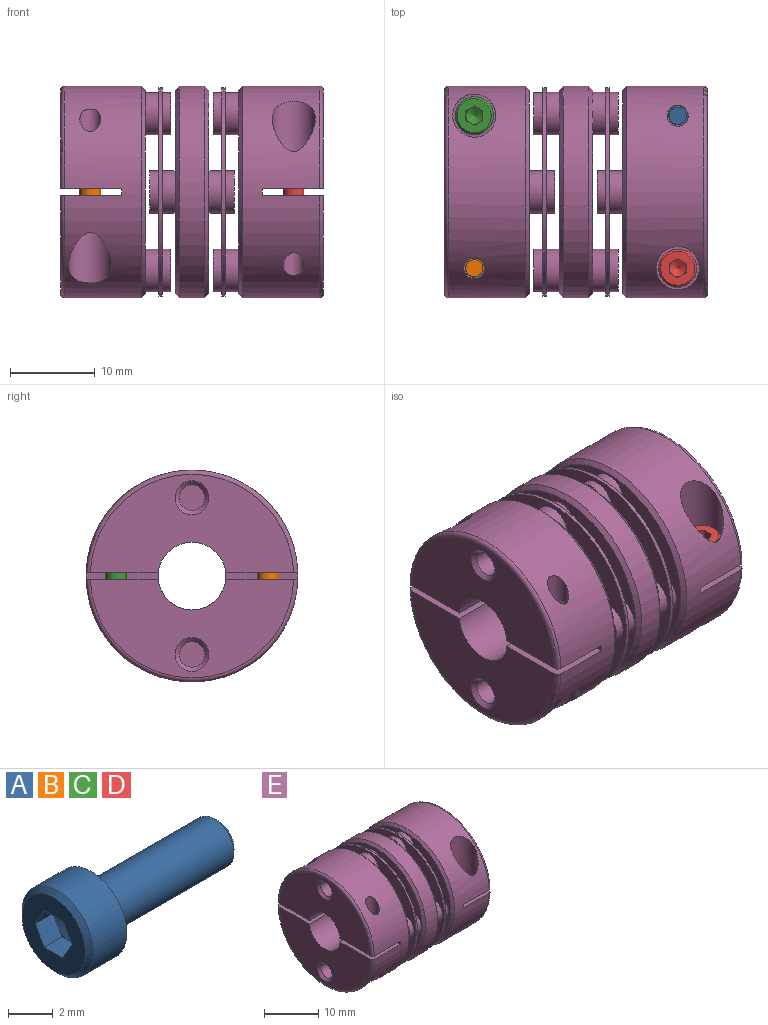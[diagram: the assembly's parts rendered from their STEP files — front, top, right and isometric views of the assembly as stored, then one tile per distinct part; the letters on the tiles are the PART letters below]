
ASSEMBLY  parts=5 mates=4
PART A: 20 faces, bbox 10.4x4.5x4.5 mm
  f0: plane 0.87x0.5mm, normal (-1,0,0), area 0.1mm2, adj f13,f14,f19
  f1: plane 1x0.29mm, normal (-1,0,0), area 0.1mm2, adj f13,f18,f19
  f2: plane 0.87x0.5mm, normal (-1,0,0), area 0.1mm2, adj f17,f18,f19
  f3: plane 0.87x0.5mm, normal (-1,0,0), area 0.1mm2, adj f16,f17,f19
  f4: plane 1x0.29mm, normal (-1,0,0), area 0.1mm2, adj f15,f16,f19
  f5: plane 0.87x0.5mm, normal (-1,0,0), area 0.1mm2, adj f14,f15,f19
  f6: plane 4x4mm, normal (-1,0,0), area 9.1mm2, adj f7,f13,f14,f15,f16,f17,f18
  f7: cone r=2.25mm half-angle=45deg, axis (1,0,0), area 4.7mm2, adj f6,f8
  f8: cylinder r=2.25mm len=4.5mm, axis (-1,0,0), area 29.8mm2, adj f7,f9
  f9: plane 4.5x4.5mm, normal (1,0,0), area 11mm2, adj f8,f10
  f10: cylinder r=1.25mm len=7.76mm, axis (-1,0,0), area 60.9mm2, adj f9,f11
  f11: cone r=1.01mm half-angle=45deg, axis (-1,0,0), area 2.4mm2, adj f10,f12
  f12: plane 2.01x2.01mm, normal (1,0,0), area 3.2mm2, adj f11
  f13: plane 1.1x1mm, normal (0,-0.87,-0.5), area 1.3mm2, adj f0,f1,f6,f14,f18
  f14: plane 1.15x1.1mm, normal (0,0,-1), area 1.3mm2, adj f0,f5,f6,f13,f15
  f15: plane 1.1x1mm, normal (0,0.87,-0.5), area 1.3mm2, adj f4,f5,f6,f14,f16
  f16: plane 1.1x1mm, normal (0,0.87,0.5), area 1.3mm2, adj f3,f4,f6,f15,f17
  f17: plane 1.15x1.1mm, normal (0,0,1), area 1.3mm2, adj f2,f3,f6,f16,f18
  f18: plane 1.1x1mm, normal (0,-0.87,0.5), area 1.3mm2, adj f1,f2,f6,f13,f17
  f19: cone r=0mm half-angle=60deg, axis (-1,0,0), area 3.6mm2, adj f0,f1,f2,f3,f4,f5
PART B: same geometry as A
PART C: same geometry as A
PART D: same geometry as A
PART E: 106 faces, bbox 31x27.1x27.1 mm
  f0: cylinder r=12.5mm len=25mm, axis (-1,0,0), area 619.5mm2, adj f1,f2,f3,f4,f14,f58,f61,f64
  f1: plane 8.52x7.21mm, normal (0,0,-1), area 56.3mm2, adj f0,f13,f60,f61,f64,f104
  f2: plane 8.52x7.21mm, normal (0,0,1), area 56.3mm2, adj f0,f12,f14,f60,f64,f99
  f3: plane 8.52x7.21mm, normal (0,0,1), area 56.3mm2, adj f0,f12,f14,f60,f65,f97
  f4: plane 8.52x7.21mm, normal (0,0,-1), area 56.3mm2, adj f0,f13,f60,f61,f65,f92
  f5: cylinder r=12.5mm len=25mm, axis (-1,0,0), area 619.5mm2, adj f6,f7,f8,f9,f16,f17,f24,f62
  f6: plane 8.52x7.21mm, normal (0,0,1), area 56.3mm2, adj f5,f10,f15,f17,f62,f91
  f7: plane 8.52x7.21mm, normal (0,0,-1), area 56.3mm2, adj f5,f11,f15,f16,f62,f87
  f8: plane 8.52x7.21mm, normal (0,0,-1), area 56.3mm2, adj f5,f11,f15,f16,f63,f84
  f9: plane 8.52x7.21mm, normal (0,0,1), area 56.3mm2, adj f5,f10,f15,f17,f63,f80
  f10: plane 23.99x11.6mm, normal (-1,0,0), area 182.1mm2, adj f6,f9,f15,f17,f75
  f11: plane 23.99x11.6mm, normal (-1,0,0), area 182.1mm2, adj f7,f8,f15,f16,f72
  f12: plane 23.99x11.6mm, normal (1,0,0), area 182.1mm2, adj f2,f3,f14,f60,f71
  f13: plane 23.99x11.6mm, normal (1,0,0), area 182.1mm2, adj f1,f4,f60,f61,f68
  f14: torus R=12mm, axis (-1,0,0), area 29.8mm2, adj f0,f2,f3,f12
  f15: cylinder r=4mm len=10mm, axis (-1,0,0), area 239.8mm2, adj f6,f7,f8,f9,f10,f11,f23,f62
  f16: torus R=12mm, axis (-1,0,0), area 29.8mm2, adj f5,f7,f8,f11
  f17: torus R=12mm, axis (-1,0,0), area 29.8mm2, adj f5,f6,f9,f10
  f18: cylinder r=2.5mm len=5mm, axis (-1,0,0), area 23.6mm2, adj f20,f44
  f19: cylinder r=2.5mm len=5mm, axis (-1,0,0), area 23.6mm2, adj f20,f44
  f20: plane 24x24mm, normal (1,0,0), area 290.4mm2, adj f18,f19,f40,f41
  f21: cylinder r=2.5mm len=5mm, axis (-1,0,0), area 25.1mm2, adj f23,f25
  f22: cylinder r=2.5mm len=5mm, axis (-1,0,0), area 25.1mm2, adj f23,f25
  f23: plane 24x24mm, normal (1,0,0), area 362.9mm2, adj f15,f21,f22,f24
  f24: cone r=12mm half-angle=45deg, axis (-1,0,0), area 54.4mm2, adj f5,f23
  f25: plane 24.6x24.6mm, normal (-1,0,0), area 274mm2, adj f21,f22,f27,f28,f34,f37
  f26: plane 24.6x24.6mm, normal (1,0,0), area 274mm2, adj f27,f28,f30,f32,f33,f36
  f27: cylinder r=12.3mm len=24.6mm, axis (-1,0,0), area 30.9mm2, adj f25,f26
  f28: cylinder r=6.25mm len=12.5mm, axis (-1,0,0), area 15.7mm2, adj f25,f26
  f29: plane 5x5mm, normal (1,0,0), area 19.6mm2, adj f30
  f30: cylinder r=2.5mm len=5mm, axis (-1,0,0), area 15.7mm2, adj f26,f29
  f31: plane 5x5mm, normal (1,0,0), area 19.6mm2, adj f32
  f32: cylinder r=2.5mm len=5mm, axis (-1,0,0), area 15.7mm2, adj f26,f31
  f33: cylinder r=2.5mm len=5mm, axis (1,0,0), area 23.6mm2, adj f26,f39
  f34: cylinder r=2.5mm len=5mm, axis (1,0,0), area 17.3mm2, adj f25,f35
  f35: plane 5x5mm, normal (-1,0,0), area 19.6mm2, adj f34
  f36: cylinder r=2.5mm len=5mm, axis (1,0,0), area 23.6mm2, adj f26,f39
  f37: cylinder r=2.5mm len=5mm, axis (1,0,0), area 17.3mm2, adj f25,f38
  f38: plane 5x5mm, normal (-1,0,0), area 19.6mm2, adj f37
  f39: plane 24x24mm, normal (-1,0,0), area 290.4mm2, adj f33,f36,f40,f43
  f40: cylinder r=6.25mm len=12.5mm, axis (-1,0,0), area 157.1mm2, adj f20,f39
  f41: cone r=12mm half-angle=45deg, axis (-1,0,0), area 54.4mm2, adj f20,f42
  f42: cylinder r=12.5mm len=25mm, axis (-1,0,0), area 235.6mm2, adj f41,f43
  f43: cone r=12.5mm half-angle=45deg, axis (1,0,0), area 54.4mm2, adj f39,f42
  f44: plane 24.6x24.6mm, normal (-1,0,0), area 274mm2, adj f18,f19,f46,f47,f53,f56
  f45: plane 24.6x24.6mm, normal (1,0,0), area 274mm2, adj f46,f47,f49,f51,f52,f55
  f46: cylinder r=12.3mm len=24.6mm, axis (-1,0,0), area 30.9mm2, adj f44,f45
  f47: cylinder r=6.25mm len=12.5mm, axis (-1,0,0), area 15.7mm2, adj f44,f45
  f48: plane 5x5mm, normal (1,0,0), area 19.6mm2, adj f49
  f49: cylinder r=2.5mm len=5mm, axis (-1,0,0), area 17.3mm2, adj f45,f48
  f50: plane 5x5mm, normal (1,0,0), area 19.6mm2, adj f51
  f51: cylinder r=2.5mm len=5mm, axis (-1,0,0), area 17.3mm2, adj f45,f50
  f52: cylinder r=2.5mm len=5mm, axis (1,0,0), area 25.1mm2, adj f45,f59
  f53: cylinder r=2.5mm len=5mm, axis (1,0,0), area 15.7mm2, adj f44,f54
  f54: plane 5x5mm, normal (-1,0,0), area 19.6mm2, adj f53
  f55: cylinder r=2.5mm len=5mm, axis (1,0,0), area 25.1mm2, adj f45,f59
  f56: cylinder r=2.5mm len=5mm, axis (1,0,0), area 15.7mm2, adj f44,f57
  f57: plane 5x5mm, normal (-1,0,0), area 19.6mm2, adj f56
  f58: cone r=12.5mm half-angle=45deg, axis (1,0,0), area 54.4mm2, adj f0,f59
  f59: plane 24x24mm, normal (-1,0,0), area 362.9mm2, adj f52,f55,f58,f60
  f60: cylinder r=4mm len=10mm, axis (-1,0,0), area 239.8mm2, adj f1,f2,f3,f4,f12,f13,f59,f64
  f61: torus R=12mm, axis (-1,0,0), area 29.8mm2, adj f0,f1,f4,f13
  f62: plane 8.52x0.8mm, normal (-1,0,0), area 6.8mm2, adj f5,f6,f7,f15
  f63: plane 8.52x0.8mm, normal (-1,0,0), area 6.8mm2, adj f5,f8,f9,f15
  f64: plane 8.52x0.8mm, normal (1,0,0), area 6.8mm2, adj f0,f1,f2,f60
  f65: plane 8.52x0.8mm, normal (1,0,0), area 6.8mm2, adj f0,f3,f4,f60
  f66: plane 3x3mm, normal (1,0,0), area 7.1mm2, adj f67
  f67: cylinder r=1.5mm len=4.5mm, axis (-1,0,0), area 42.4mm2, adj f66,f68
  f68: cone r=2mm half-angle=45deg, axis (1,0,0), area 7.8mm2, adj f13,f67
  f69: plane 3x3mm, normal (1,0,0), area 7.1mm2, adj f70
  f70: cylinder r=1.5mm len=4.5mm, axis (-1,0,0), area 42.4mm2, adj f69,f71
  f71: cone r=2mm half-angle=45deg, axis (1,0,0), area 7.8mm2, adj f12,f70
  f72: cone r=1.5mm half-angle=45deg, axis (-1,0,0), area 7.8mm2, adj f11,f73
  f73: cylinder r=1.5mm len=4.5mm, axis (-1,0,0), area 42.4mm2, adj f72,f74
  f74: plane 3x3mm, normal (-1,0,0), area 7.1mm2, adj f73
  f75: cone r=1.5mm half-angle=45deg, axis (-1,0,0), area 7.8mm2, adj f10,f76
  f76: cylinder r=1.5mm len=4.5mm, axis (-1,0,0), area 42.4mm2, adj f75,f77
  f77: plane 3x3mm, normal (-1,0,0), area 7.1mm2, adj f76
  f78: cylinder r=2.55mm len=8.71mm, axis (0,0,1), area 99.8mm2, adj f5,f79
  f79: plane 5.1x5.1mm, normal (0,0,-1), area 15.5mm2, adj f78,f80
  f80: cylinder r=1.25mm len=2.5mm, axis (0,0,1), area 12.6mm2, adj f9,f79
  f81: cylinder r=1.25mm len=3.81mm, axis (0,0,1), area 20.3mm2, adj f5,f82
  f82: cone r=1.01mm half-angle=45deg, axis (0,0,1), area 2.4mm2, adj f81,f83
  f83: cylinder r=1.01mm len=5.11mm, axis (0,0,1), area 32.3mm2, adj f82,f84
  f84: cone r=1.25mm half-angle=45deg, axis (0,0,-1), area 2.4mm2, adj f8,f83
  f85: cylinder r=2.55mm len=8.71mm, axis (0,0,-1), area 99.8mm2, adj f5,f86
  f86: plane 5.1x5.1mm, normal (0,0,1), area 15.5mm2, adj f85,f87
  f87: cylinder r=1.25mm len=2.5mm, axis (0,0,-1), area 12.6mm2, adj f7,f86
  f88: cylinder r=1.25mm len=3.81mm, axis (0,0,-1), area 20.3mm2, adj f5,f89
  f89: cone r=1.01mm half-angle=45deg, axis (0,0,-1), area 2.4mm2, adj f88,f90
  f90: cylinder r=1.01mm len=5.11mm, axis (0,0,-1), area 32.3mm2, adj f89,f91
  f91: cone r=1.25mm half-angle=45deg, axis (0,0,1), area 2.4mm2, adj f6,f90
  f92: cone r=1.25mm half-angle=45deg, axis (0,0,-1), area 2.4mm2, adj f4,f93
  f93: cylinder r=1.01mm len=5.11mm, axis (0,0,1), area 32.3mm2, adj f92,f94
  f94: cone r=1.01mm half-angle=45deg, axis (0,0,1), area 2.4mm2, adj f93,f95
  f95: cylinder r=1.25mm len=3.81mm, axis (0,0,1), area 20.3mm2, adj f0,f94
  f96: cylinder r=2.55mm len=8.71mm, axis (0,0,1), area 99.8mm2, adj f0,f98
  f97: cylinder r=1.25mm len=2.5mm, axis (0,0,1), area 12.6mm2, adj f3,f98
  f98: plane 5.1x5.1mm, normal (0,0,-1), area 15.5mm2, adj f96,f97
  f99: cone r=1.25mm half-angle=45deg, axis (0,0,1), area 2.4mm2, adj f2,f100
  f100: cylinder r=1.01mm len=5.11mm, axis (0,0,-1), area 32.3mm2, adj f99,f101
  f101: cone r=1.01mm half-angle=45deg, axis (0,0,-1), area 2.4mm2, adj f100,f102
  f102: cylinder r=1.25mm len=3.81mm, axis (0,0,-1), area 20.3mm2, adj f0,f101
  f103: cylinder r=2.55mm len=8.71mm, axis (0,0,-1), area 99.8mm2, adj f0,f105
  f104: cylinder r=1.25mm len=2.5mm, axis (0,0,-1), area 12.6mm2, adj f1,f105
  f105: plane 5.1x5.1mm, normal (0,0,1), area 15.5mm2, adj f103,f104
PLACE A rot(axis=(0,-1,0),90deg) t=(16.4,9.84,-4.55)mm
PLACE B rot(axis=(0,-1,0),90deg) t=(-7.6,-8.16,-4.55)mm
PLACE C rot(axis=(0.71,0,-0.71),180deg) t=(-7.6,9.84,-0.55)mm
PLACE D rot(axis=(0.71,0,-0.71),180deg) t=(16.4,-8.16,-0.55)mm
PLACE E t=(-11.1,0.84,-2.55)mm
MATE revolute A.f7 <-> E.f92  axis (0,0,1) through (16.4,9.84,-4.55)mm
MATE revolute D.f7 <-> E.f99  axis (0,0,-1) through (16.4,-8.16,-0.55)mm
MATE revolute C.f7 <-> E.f85  axis (0,0,-1) through (-7.6,9.84,-0.55)mm
MATE revolute B.f7 <-> E.f78  axis (0,0,1) through (-7.6,-8.16,-4.55)mm
